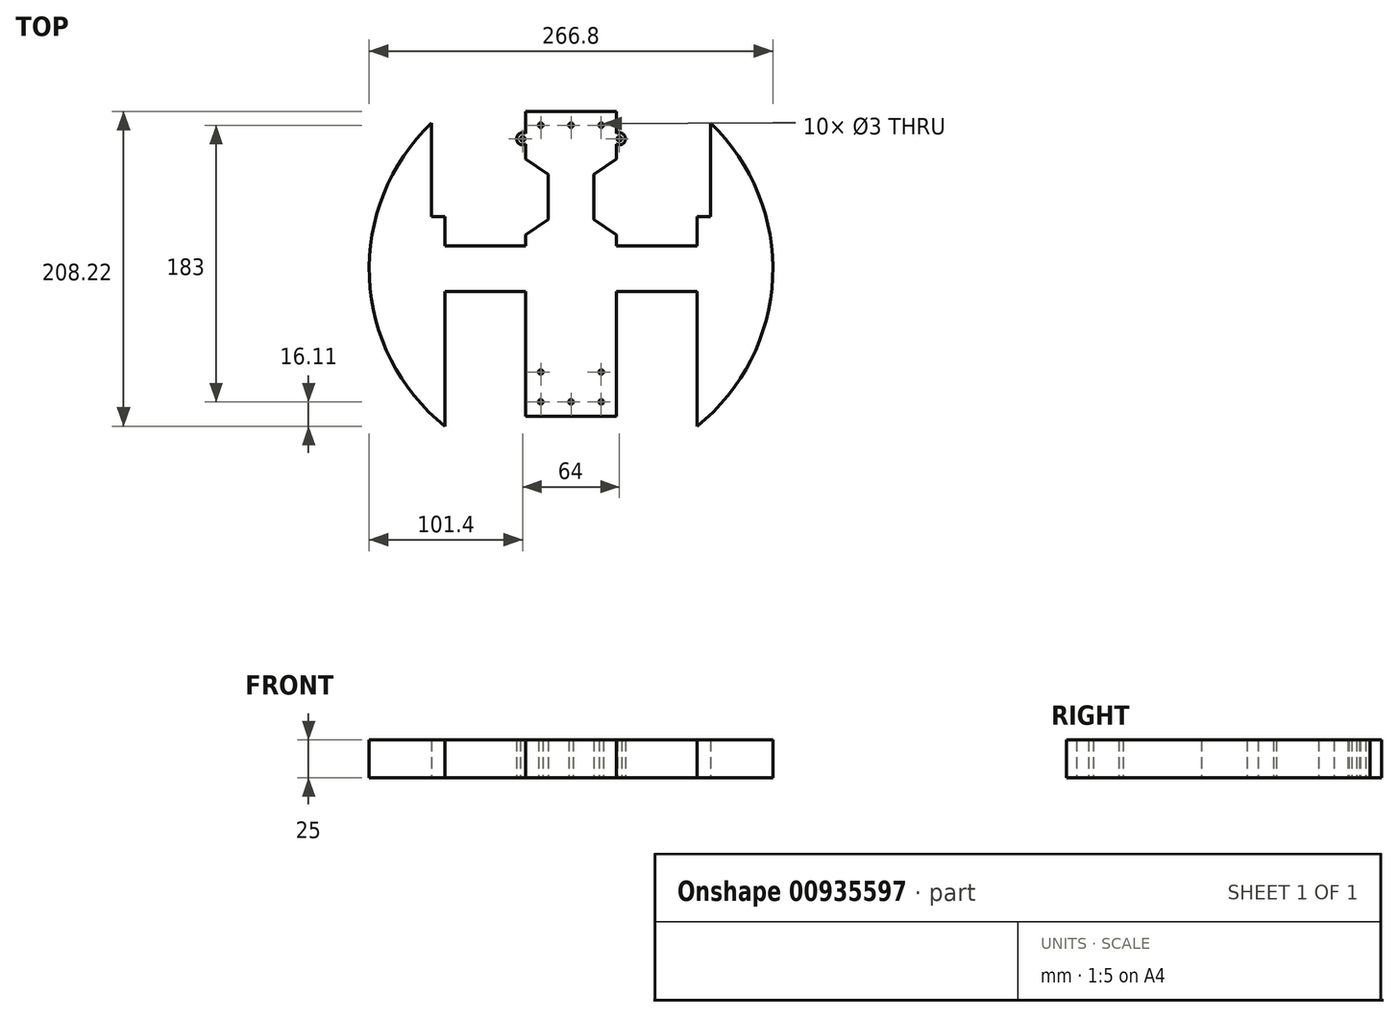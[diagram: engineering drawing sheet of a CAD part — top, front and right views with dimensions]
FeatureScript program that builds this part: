
annotation { "Feature Type Name" : "Feature", "Feature Type Description" : "" }
export const myFeature = defineFeature(function(context is Context, id is Id, definition is map)
    precondition{}
    {
        {
            var Q0;
            Q0=qCreatedBy(makeId("Top.planeOp"),FACE);
            var sketch = newSketch(context, id + "F0", { "sketchPlane" : qUnion([Q0])});
            skCircle(sketch, "E0", {"center": v(-20, -88) * mm, "radius": 1.5 * mm});
            skCircle(sketch, "E1", {"center": v(0, -88) * mm, "radius": 1.5 * mm});
            skCircle(sketch, "E2", {"center": v(20, -88) * mm, "radius": 1.5 * mm});
            skCircle(sketch, "E3", {"center": v(-20, -68.25) * mm, "radius": 1.5 * mm});
            skCircle(sketch, "E4", {"center": v(20, -68.25) * mm, "radius": 1.5 * mm});
            skCircle(sketch, "E5", {"center": v(-20, 95) * mm, "radius": 1.5 * mm});
            skCircle(sketch, "E6", {"center": v(0, 95) * mm, "radius": 1.5 * mm});
            skCircle(sketch, "E7", {"center": v(20, 95) * mm, "radius": 1.5 * mm});
            skCircle(sketch, "E8", {"center": v(-32, 86) * mm, "radius": 1.5 * mm});
            skCircle(sketch, "E9", {"center": v(32, 86) * mm, "radius": 1.5 * mm});
            skLineSegment(sketch, "E10.bottom", {"start": v(44, 104.11) * mm, "end": v(68, 104.11) * mm});
            skLineSegment(sketch, "E10.top", {"start": v(44, 40.11) * mm, "end": v(68, 40.11) * mm});
            skLineSegment(sketch, "E10.left", {"start": v(44, 104.11) * mm, "end": v(44, 40.11) * mm});
            skLineSegment(sketch, "E10.right", {"start": v(68, 104.11) * mm, "end": v(68, 40.11) * mm});
            skLineSegment(sketch, "E11.MirrorCS", {"start": v(-44, 104.11) * mm, "end": v(-44, 40.11) * mm});
            skLineSegment(sketch, "E12.MirrorCS", {"start": v(-44, 104.11) * mm, "end": v(-68, 104.11) * mm});
            skLineSegment(sketch, "E13.MirrorCS", {"start": v(-68, 104.11) * mm, "end": v(-68, 40.11) * mm});
            skLineSegment(sketch, "E14.MirrorCS", {"start": v(-44, 40.11) * mm, "end": v(-68, 40.11) * mm});
            skLineSegment(sketch, "E15.bottom", {"start": v(-80, -33.42) * mm, "end": v(-44, -33.42) * mm});
            skLineSegment(sketch, "E15.top", {"start": v(-80, -97.42) * mm, "end": v(-44, -97.42) * mm});
            skLineSegment(sketch, "E15.left", {"start": v(-80, -33.42) * mm, "end": v(-80, -97.42) * mm});
            skLineSegment(sketch, "E15.right", {"start": v(-44, -33.42) * mm, "end": v(-44, -97.42) * mm});
            skLineSegment(sketch, "E16.MirrorCS", {"start": v(44, -33.42) * mm, "end": v(44, -97.42) * mm});
            skLineSegment(sketch, "E17.MirrorCS", {"start": v(80, -33.42) * mm, "end": v(44, -33.42) * mm});
            skLineSegment(sketch, "E18.MirrorCS", {"start": v(80, -33.42) * mm, "end": v(80, -97.42) * mm});
            skLineSegment(sketch, "E19.MirrorCS", {"start": v(80, -97.42) * mm, "end": v(44, -97.42) * mm});
            skArc(sketch, "E20", {"start": v(-92.2, 96.4) * mm, "mid": v(-133.27, -5.86) * mm, "end": v(-83.4, -104.11) * mm});
            skLineSegment(sketch, "E21", {"start": v(-80, -106.74) * mm, "end": v(-80, -97.42) * mm});
            skLineSegment(sketch, "E22", {"start": v(-80, -97.42) * mm, "end": v(80, -97.42) * mm});
            skLineSegment(sketch, "E23", {"start": v(80, -97.42) * mm, "end": v(80, -106.74) * mm});
            skLineSegment(sketch, "E24", {"start": v(68, 104.11) * mm, "end": v(44, 104.11) * mm});
            skLineSegment(sketch, "E25", {"start": v(83.4, -104.11) * mm, "end": v(83.4, -15.02) * mm});
            skLineSegment(sketch, "E26", {"start": v(-83.4, 34.4) * mm, "end": v(-83.4, 15.02) * mm});
            skLineSegment(sketch, "E27", {"start": v(-83.4, 15.02) * mm, "end": v(-30, 15.02) * mm});
            skLineSegment(sketch, "E28.MirrorCS", {"start": v(-83.4, -15.02) * mm, "end": v(-30, -15.02) * mm});
            skLineSegment(sketch, "E29.MirrorCS", {"start": v(83.4, 15.02) * mm, "end": v(30, 15.02) * mm});
            skLineSegment(sketch, "E30.MirrorCS", {"start": v(83.4, -15.02) * mm, "end": v(30, -15.02) * mm});
            skArc(sketch, "E31.trimOffspring", {"start": v(83.4, -104.11) * mm, "mid": v(133.27, -5.86) * mm, "end": v(92.2, 96.4) * mm});
            skLineSegment(sketch, "E32", {"start": v(-30, -15.02) * mm, "end": v(-30, -97.42) * mm});
            skLineSegment(sketch, "E33", {"start": v(30, -15.02) * mm, "end": v(30, -97.42) * mm});
            skLineSegment(sketch, "E34", {"start": v(30, 15.02) * mm, "end": v(30, 22.54) * mm});
            skLineSegment(sketch, "E35", {"start": v(-30, 15.02) * mm, "end": v(-30, 22.54) * mm});
            skPoint(sketch, "E36.start.orphan", {"position": v(-21.78, 104.11) * mm});
            skPoint(sketch, "E37.end.orphan", {"position": v(21.78, 104.11) * mm});
            skLineSegment(sketch, "E38.trimOffspring", {"start": v(83.4, 15.02) * mm, "end": v(83.4, 34.4) * mm});
            skLineSegment(sketch, "E39.trimOffspring", {"start": v(-83.4, -15.02) * mm, "end": v(-83.4, -104.11) * mm});
            skLineSegment(sketch, "E40.trimOffspring", {"start": v(30, 104.11) * mm, "end": v(-30, 104.11) * mm});
            skArc(sketch, "E41", {"start": v(30, 82.54) * mm, "mid": v(36, 86) * mm, "end": v(30, 89.46) * mm});
            skLineSegment(sketch, "E42.trimOffspring", {"start": v(30, 89.46) * mm, "end": v(30, 104.11) * mm});
            skArc(sketch, "E43.MirrorCS", {"start": v(-30, 82.54) * mm, "mid": v(-36, 86) * mm, "end": v(-30, 89.46) * mm});
            skLineSegment(sketch, "E44.trimOffspring", {"start": v(-30, 89.46) * mm, "end": v(-30, 104.11) * mm});
            skLineSegment(sketch, "E45", {"start": v(-30, 72.54) * mm, "end": v(-15, 62.54) * mm});
            skLineSegment(sketch, "E46", {"start": v(-15, 62.54) * mm, "end": v(-15, 32.54) * mm});
            skLineSegment(sketch, "E47", {"start": v(-15, 32.54) * mm, "end": v(-30, 22.54) * mm});
            skLineSegment(sketch, "E48", {"start": v(-92.2, 96.4) * mm, "end": v(-92.2, 34.4) * mm});
            skLineSegment(sketch, "E49", {"start": v(-92.2, 34.4) * mm, "end": v(-83.4, 34.4) * mm});
            skLineSegment(sketch, "E50.trimOffspring", {"start": v(-30, 72.54) * mm, "end": v(-30, 82.54) * mm});
            skLineSegment(sketch, "E51.MirrorCS", {"start": v(15, 62.54) * mm, "end": v(15, 32.54) * mm});
            skLineSegment(sketch, "E52.MirrorCS", {"start": v(30, 72.54) * mm, "end": v(15, 62.54) * mm});
            skLineSegment(sketch, "E53.MirrorCS", {"start": v(15, 32.54) * mm, "end": v(30, 22.54) * mm});
            skLineSegment(sketch, "E54.MirrorCS", {"start": v(92.2, 96.4) * mm, "end": v(92.2, 34.4) * mm});
            skLineSegment(sketch, "E55.MirrorCS", {"start": v(92.2, 34.4) * mm, "end": v(83.4, 34.4) * mm});
            skLineSegment(sketch, "E56.trimOffspring", {"start": v(30, 72.54) * mm, "end": v(30, 82.54) * mm});
            skPoint(sketch, "E57.orphan", {"position": v(83.4, 104.11) * mm});
            skSolve(sketch);
        }
        {
            var Q0;
            Q0=makeQuery(id+"F0.imprint","IMPRINT",FACE,{"disambiguationData":[TD([[makeQuery(id+"F0.imprint","IMPRINT",EDGE,{"derivedFrom":sQuery(id+"F0.wireOp",EDGE,"E0")}),-1.0]])]});
            extrude(context, id + "F1", {"entities" : qUnion([Q0]), "depth" : 25 * mm, "offsetDistance" : 25 * mm});
        }
    });
